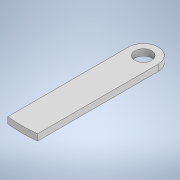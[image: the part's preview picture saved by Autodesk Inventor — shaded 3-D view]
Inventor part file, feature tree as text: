
AUTODESK INVENTOR PART (.ipt)
format: ipt  version: 2021 (Build 250183000, 183)  size: 100,864 bytes
history: native  units: mm
features: extrude x2, sketch x2
ambient origin geometry x8: Origin, YZ Plane, XZ Plane, XY Plane, X Axis, Y Axis, Z Axis, Center Point
bodies: Solid1 (feature_tree)
feature tree (4):
  extrude  "Extrusion1"  Depth=9.398mm
  extrude  "Extrusion2"  Depth=2.0mm
  sketch  "Sketch1"  dims[d0=76.778mm d1=9.398mm]
  sketch  "Sketch2"  dims[d2=2.0mm d3=0.0mm d4=5.3mm d5=0.0mm d6=0.0mm]
